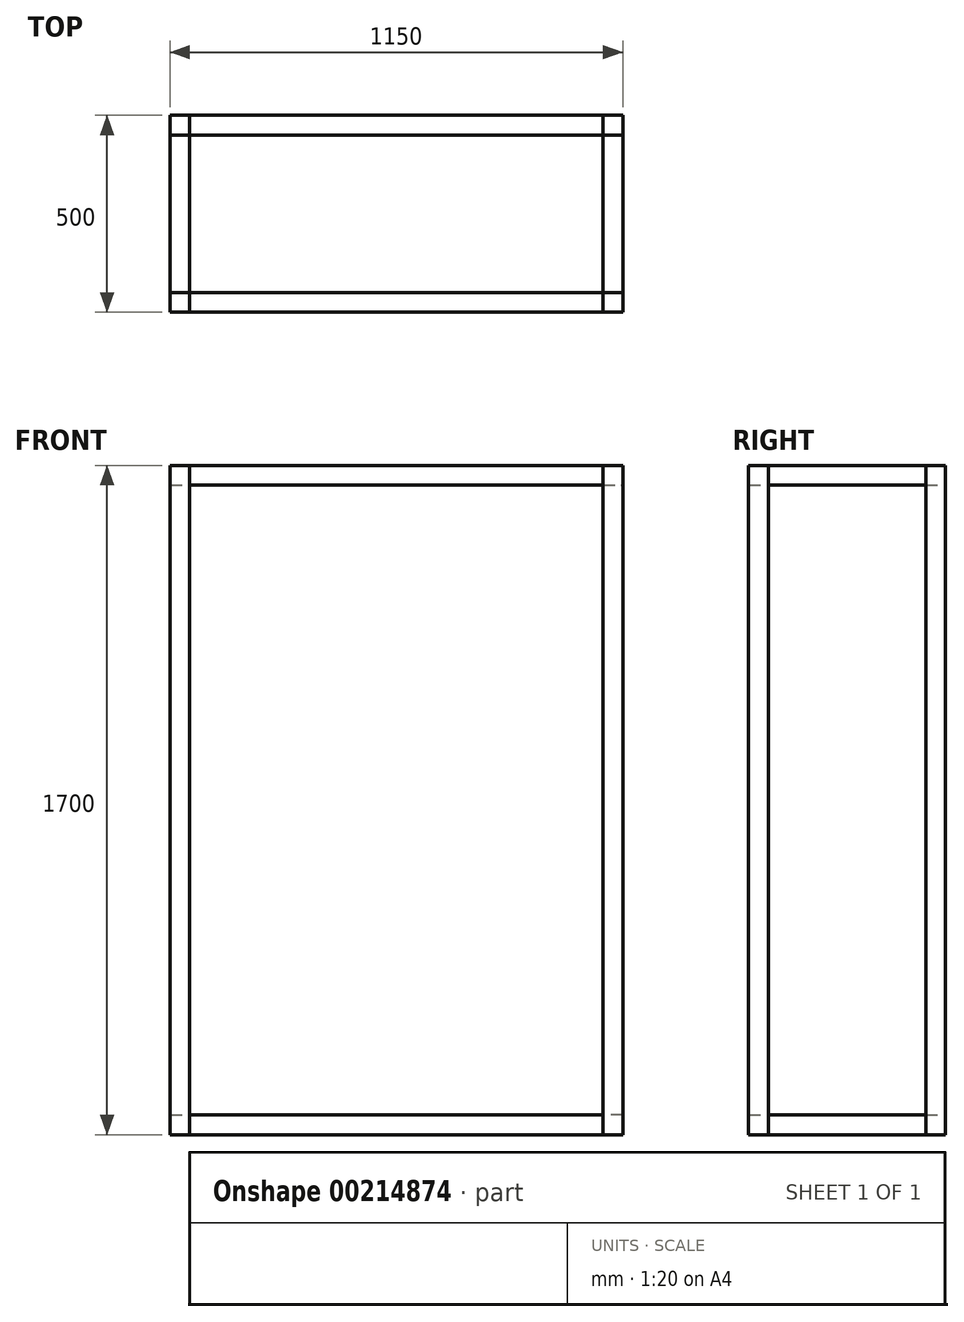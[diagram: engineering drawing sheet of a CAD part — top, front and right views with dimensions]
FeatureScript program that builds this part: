
annotation { "Feature Type Name" : "Feature", "Feature Type Description" : "" }
export const myFeature = defineFeature(function(context is Context, id is Id, definition is map)
    precondition{}
    {
        {
            var Q0;
            Q0=qCreatedBy(makeId("Front.planeOp"),FACE);
            var sketch = newSketch(context, id + "F0", { "sketchPlane" : qUnion([Q0])});
            skLineSegment(sketch, "E0.bottom", {"start": v(-575, 0) * mm, "end": v(-525, 0) * mm});
            skLineSegment(sketch, "E0.top", {"start": v(-575, 1700) * mm, "end": v(-525, 1700) * mm});
            skLineSegment(sketch, "E0.left", {"start": v(-575, 0) * mm, "end": v(-575, 1700) * mm});
            skLineSegment(sketch, "E0.right", {"start": v(-525, 0) * mm, "end": v(-525, 1700) * mm});
            skLineSegment(sketch, "E1.bottom", {"start": v(-524.9, 1700) * mm, "end": v(524.9, 1700) * mm});
            skLineSegment(sketch, "E1.top", {"start": v(-524.9, 1650) * mm, "end": v(524.9, 1650) * mm});
            skLineSegment(sketch, "E1.left", {"start": v(-524.9, 1700) * mm, "end": v(-524.9, 1650) * mm});
            skLineSegment(sketch, "E1.right", {"start": v(524.9, 1700) * mm, "end": v(524.9, 1650) * mm});
            skLineSegment(sketch, "E2.bottom", {"start": v(-524.9, 0) * mm, "end": v(524.9, 0) * mm});
            skLineSegment(sketch, "E2.top", {"start": v(-524.9, 50) * mm, "end": v(524.9, 50) * mm});
            skLineSegment(sketch, "E2.left", {"start": v(-524.9, 0) * mm, "end": v(-524.9, 50) * mm});
            skLineSegment(sketch, "E2.right", {"start": v(524.9, 0) * mm, "end": v(524.9, 50) * mm});
            skLineSegment(sketch, "E3.bottom", {"start": v(525, 1700) * mm, "end": v(575, 1700) * mm});
            skLineSegment(sketch, "E3.top", {"start": v(525, 0) * mm, "end": v(575, 0) * mm});
            skLineSegment(sketch, "E3.left", {"start": v(525, 1700) * mm, "end": v(525, 0) * mm});
            skLineSegment(sketch, "E3.right", {"start": v(575, 1700) * mm, "end": v(575, 0) * mm});
            skSolve(sketch);
        }
        {
            var Q0;
            Q0 = qSketchRegion(id + "F0", true);
            extrude(context, id + "F1", {"entities" : qUnion([Q0]), "depth" : 50 * mm, "offsetDistance" : 25 * mm});
        }
        {
            var Q0;
            Q0=makeQuery(id+"F1.opExtrude","CAP_FACE",FACE,{"disambiguationData":[OSD([sQuery(id+"F0.wireOp",EDGE,"E0.bottom"),sQuery(id+"F0.wireOp",EDGE,"E0.top"),sQuery(id+"F0.wireOp",EDGE,"E0.left"),sQuery(id+"F0.wireOp",EDGE,"E0.right")])],"isStart":false});
            var sketch = newSketch(context, id + "F2", { "sketchPlane" : qUnion([Q0])});
            skLineSegment(sketch, "E4.0", {"start": v(-575, 1700) * mm, "end": v(-525, 1700) * mm, "construction": true});
            skLineSegment(sketch, "E5.0", {"start": v(525, 1700) * mm, "end": v(575, 1700) * mm, "construction": true});
            skLineSegment(sketch, "E6.0", {"start": v(525, 0) * mm, "end": v(575, 0) * mm, "construction": true});
            skLineSegment(sketch, "E7.0", {"start": v(-575, 0) * mm, "end": v(-525, 0) * mm, "construction": true});
            skLineSegment(sketch, "E8.bottom", {"start": v(-575, 1700) * mm, "end": v(-525, 1700) * mm});
            skLineSegment(sketch, "E8.top", {"start": v(-575, 1650) * mm, "end": v(-525, 1650) * mm});
            skLineSegment(sketch, "E8.left", {"start": v(-575, 1700) * mm, "end": v(-575, 1650) * mm});
            skLineSegment(sketch, "E8.right", {"start": v(-525, 1700) * mm, "end": v(-525, 1650) * mm});
            skLineSegment(sketch, "E9.bottom", {"start": v(525, 1700) * mm, "end": v(575, 1700) * mm});
            skLineSegment(sketch, "E9.top", {"start": v(525, 1650) * mm, "end": v(575, 1650) * mm});
            skLineSegment(sketch, "E9.left", {"start": v(525, 1700) * mm, "end": v(525, 1650) * mm});
            skLineSegment(sketch, "E9.right", {"start": v(575, 1700) * mm, "end": v(575, 1650) * mm});
            skLineSegment(sketch, "E10.bottom", {"start": v(575, 0) * mm, "end": v(525, 0) * mm});
            skLineSegment(sketch, "E10.top", {"start": v(575, 50) * mm, "end": v(525, 50) * mm});
            skLineSegment(sketch, "E10.left", {"start": v(575, 0) * mm, "end": v(575, 50) * mm});
            skLineSegment(sketch, "E10.right", {"start": v(525, 0) * mm, "end": v(525, 50) * mm});
            skLineSegment(sketch, "E11.bottom", {"start": v(-575, 0) * mm, "end": v(-525, 0) * mm});
            skLineSegment(sketch, "E11.top", {"start": v(-575, 50) * mm, "end": v(-525, 50) * mm});
            skLineSegment(sketch, "E11.left", {"start": v(-575, 0) * mm, "end": v(-575, 50) * mm});
            skLineSegment(sketch, "E11.right", {"start": v(-525, 0) * mm, "end": v(-525, 50) * mm});
            skSolve(sketch);
        }
        {
            var Q0;
            Q0 = qSketchRegion(id + "F2", true);
            extrude(context, id + "F3", {"entities" : qUnion([Q0]), "depth" : 400 * mm, "offsetDistance" : 25 * mm});
        }
        {
            var Q0;
            Q0=makeQuery(id+"F1.opExtrude","SWEPT_BODY",BODY,{"disambiguationData":[OSD([sQuery(id+"F0.wireOp",EDGE,"E0.bottom"),sQuery(id+"F0.wireOp",EDGE,"E0.top"),sQuery(id+"F0.wireOp",EDGE,"E0.left"),sQuery(id+"F0.wireOp",EDGE,"E0.right")])]});
            var Q1;
            Q1=makeQuery(id+"F1.opExtrude","SWEPT_BODY",BODY,{"disambiguationData":[OSD([sQuery(id+"F0.wireOp",EDGE,"E1.bottom"),sQuery(id+"F0.wireOp",EDGE,"E1.top"),sQuery(id+"F0.wireOp",EDGE,"E1.left"),sQuery(id+"F0.wireOp",EDGE,"E1.right")])]});
            var Q2;
            Q2=makeQuery(id+"F1.opExtrude","SWEPT_BODY",BODY,{"disambiguationData":[OSD([sQuery(id+"F0.wireOp",EDGE,"E3.bottom"),sQuery(id+"F0.wireOp",EDGE,"E3.top"),sQuery(id+"F0.wireOp",EDGE,"E3.left"),sQuery(id+"F0.wireOp",EDGE,"E3.right")])]});
            var Q3;
            Q3=makeQuery(id+"F1.opExtrude","SWEPT_BODY",BODY,{"disambiguationData":[OSD([sQuery(id+"F0.wireOp",EDGE,"E2.bottom"),sQuery(id+"F0.wireOp",EDGE,"E2.top"),sQuery(id+"F0.wireOp",EDGE,"E2.left"),sQuery(id+"F0.wireOp",EDGE,"E2.right")])]});
            transform(context, id + "F4", {"entities" : qUnion([Q0, Q1, Q2, Q3]), "transformType" : TransformType.TRANSLATION_3D, "dx" : 0 * mm, "dy" : -450 * mm, "dz" : 0 * mm, "makeCopy" : true});
        }
    });
